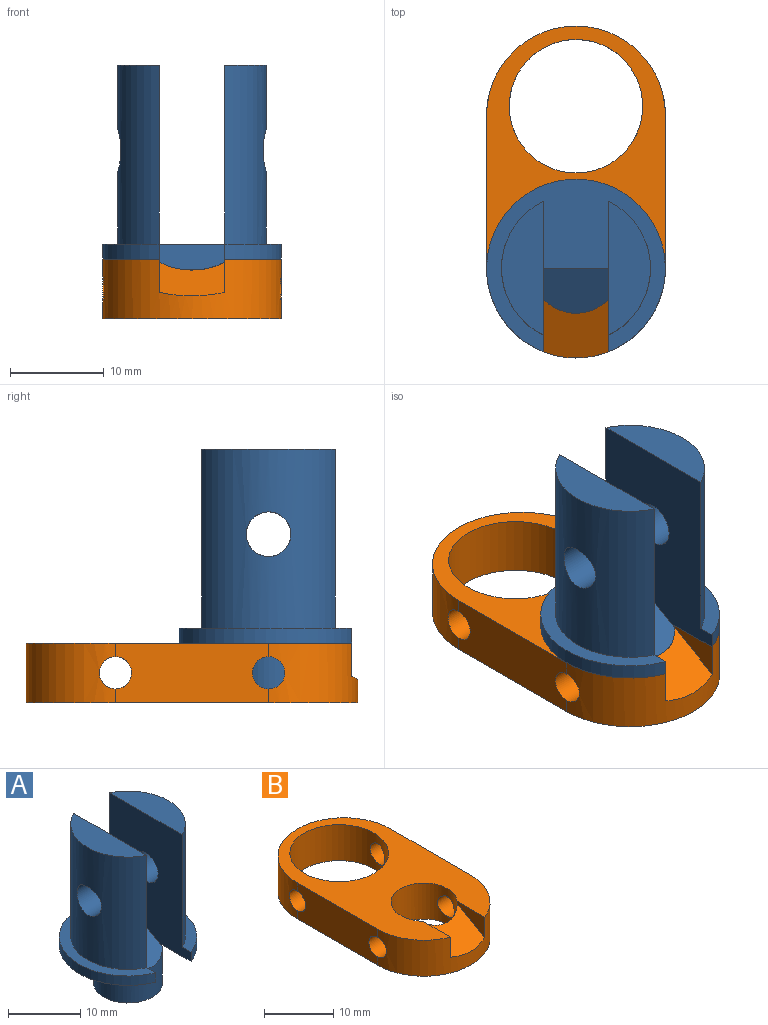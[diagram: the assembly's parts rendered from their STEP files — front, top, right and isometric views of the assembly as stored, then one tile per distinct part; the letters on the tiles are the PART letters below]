
ASSEMBLY  parts=2 mates=1
PART A: 14 faces, bbox 19.1x18.4x27 mm
  f0: cylinder r=9.53mm len=19.05mm, axis (0,0,1), area 83.7mm2, adj f1,f5,f7,f10
  f1: plane 19.05x18.39mm, normal (0,0,-1), area 178.7mm2, adj f0,f2,f5,f10
  f2: cylinder r=4.76mm len=9.53mm, axis (0,0,1), area 183.3mm2, adj f1,f5,f10,f12,f13
  f3: cylinder r=7.94mm len=19.05mm, axis (0,0,-1), area 319.2mm2, adj f4,f5,f6,f7
  f4: plane 14.26x4.45mm, normal (0,0,1), area 45.4mm2, adj f3,f5
  f5: plane 20.92x15.99mm, normal (1,0,0), area 265.7mm2, adj f0,f1,f2,f3,f4,f6,f7,f13
  f6: cylinder r=2.38mm len=4.76mm, axis (1,0,0), area 63.8mm2, adj f3,f5
  f7: plane 19.05x18.39mm, normal (0,0,1), area 129.3mm2, adj f0,f3,f5,f8,f10,f13
  f8: cylinder r=7.94mm len=19.05mm, axis (0,0,-1), area 319.2mm2, adj f7,f9,f10,f11
  f9: plane 14.26x4.45mm, normal (0,0,1), area 45.4mm2, adj f8,f10
  f10: plane 20.92x15.99mm, normal (-1,0,0), area 265.7mm2, adj f0,f1,f2,f7,f8,f9,f11,f13
  f11: cylinder r=2.38mm len=4.76mm, axis (-1,0,0), area 63.8mm2, adj f8,f10
  f12: plane 9.53x9.53mm, normal (0,0,-1), area 71.3mm2, adj f2
  f13: plane 6.99x4.76mm, normal (0,-0.5,0.87), area 34.6mm2, adj f2,f5,f7,f10
PART B: 15 faces, bbox 19.1x35.4x6.4 mm
  f0: cylinder r=9.53mm len=19.06mm, axis (0,0,1), area 153.5mm2, adj f1,f5,f6,f7,f8,f9,f12,f13
  f1: plane 16.32x6.35mm, normal (-1,0,0), area 94.2mm2, adj f0,f2,f6,f7,f8,f10
  f2: cylinder r=9.53mm len=19.06mm, axis (0,0,1), area 180.8mm2, adj f1,f5,f6,f7,f10,f11
  f3: cylinder r=7.11mm len=14.22mm, axis (0,0,1), area 264.7mm2, adj f6,f7,f10,f11
  f4: cylinder r=4.76mm len=9.53mm, axis (0,0,1), area 164.1mm2, adj f6,f7,f8,f9,f12,f13,f14
  f5: plane 16.32x6.35mm, normal (1,0,0), area 94.2mm2, adj f0,f2,f6,f7,f9,f11
  f6: plane 35.37x19.06mm, normal (0,0,-1), area 366.1mm2, adj f0,f1,f2,f3,f4,f5
  f7: plane 34.71x19.06mm, normal (0,0,1), area 331mm2, adj f0,f1,f2,f3,f4,f5,f13,f14
  f8: cylinder r=1.73mm len=5.09mm, axis (-1,0,0), area 53.1mm2, adj f0,f1,f4
  f9: cylinder r=1.73mm len=5.09mm, axis (-1,0,0), area 53mm2, adj f0,f4,f5
  f10: cylinder r=1.73mm len=3.45mm, axis (-1,0,0), area 27.7mm2, adj f1,f2,f3
  f11: cylinder r=1.73mm len=3.45mm, axis (-1,0,0), area 27.7mm2, adj f2,f3,f5
  f12: plane 6.99x6.29mm, normal (0,-0.5,0.87), area 40.4mm2, adj f0,f4,f13,f14
  f13: plane 5.62x3.54mm, normal (1,0,0), area 10.8mm2, adj f0,f4,f7,f12
  f14: plane 5.62x3.54mm, normal (-1,0,0), area 10.8mm2, adj f0,f4,f7,f12
PLACE A t=(0.96,1.86,1.17)mm
PLACE B t=(-18.1,1.86,-0.41)mm
MATE fastened B.f0 <-> A.f2  axis (0,0,-1) through (0.96,1.86,-6.76)mm
